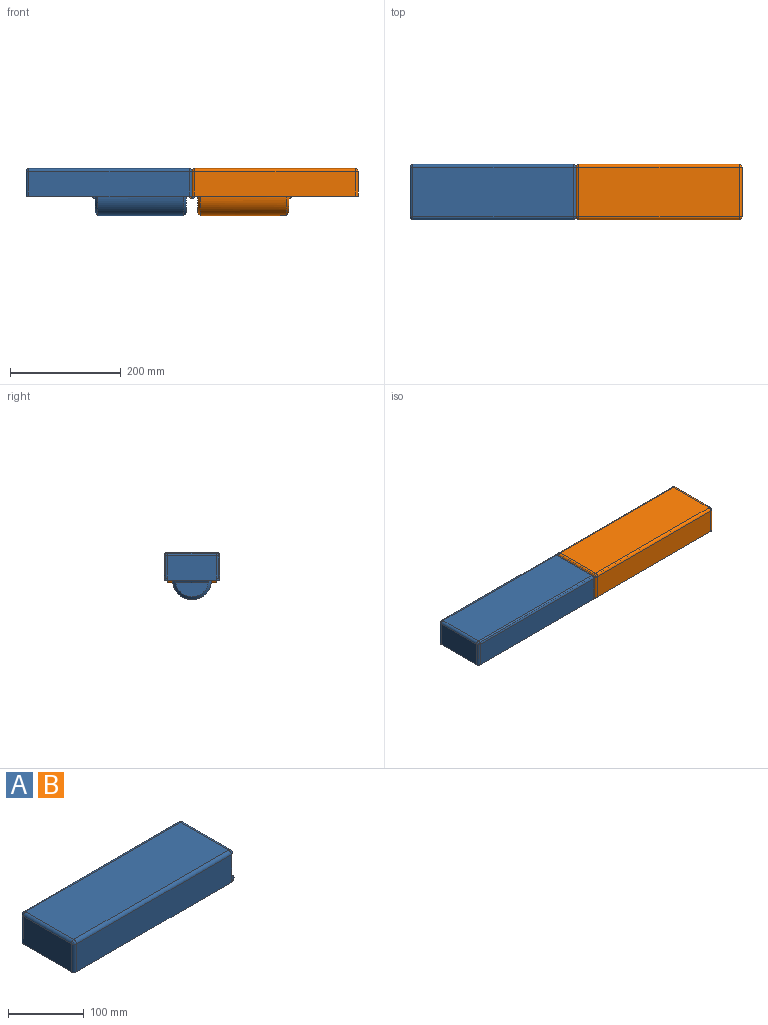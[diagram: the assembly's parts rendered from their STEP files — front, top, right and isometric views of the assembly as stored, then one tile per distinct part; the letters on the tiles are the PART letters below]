
ASSEMBLY  parts=2 mates=1
PART A: 72 faces, bbox 305x100x85 mm
  f0: plane 59.28x25.37mm, normal (-1,0,0), area 1137.1mm2, adj f18,f65
  f1: plane 9.26x0.36mm, normal (-1,0,0), area 2.2mm2, adj f18,f64
  f2: plane 9.26x0.36mm, normal (-1,0,0), area 2.2mm2, adj f18,f63
  f3: plane 45x37.5mm, normal (0,1,0), area 361.4mm2, adj f21,f22,f23,f25,f43,f44,f45,f46
  f4: plane 80x40mm, normal (-1,0,0), area 1275.8mm2, adj f10,f11,f13,f14,f15
  f5: plane 90x40mm, normal (1,0,0), area 3600mm2, adj f53,f59,f62,f70
  f6: plane 290x45mm, normal (0,1,0), area 13050mm2, adj f10,f56,f60,f62
  f7: plane 90x45mm, normal (-1,0,0), area 4050mm2, adj f10,f51,f55,f56
  f8: plane 290x45mm, normal (0,-1,0), area 13050mm2, adj f10,f51,f53,f54
  f9: plane 290x90mm, normal (0,0,1), area 26100mm2, adj f54,f55,f59,f60
  f10: plane 300x100mm, normal (0,0,-1), area 7603.5mm2, adj f4,f6,f7,f8,f11,f12,f13,f15
  f11: plane 280x40mm, normal (0,-1,0), area 11200mm2, adj f4,f10,f12,f14
  f12: plane 80x40mm, normal (1,0,0), area 2493.1mm2, adj f10,f11,f13,f14,f20
  f13: plane 280x40mm, normal (0,1,0), area 11200mm2, adj f4,f10,f12,f14
  f14: plane 280x80mm, normal (0,0,-1), area 22400mm2, adj f4,f11,f12,f13
  f15: cylinder r=35mm len=160mm, axis (1,0,0), area 34636.1mm2, adj f4,f10,f18,f19
  f16: plane 59.28x25.37mm, normal (-1,0,0), area 1137.1mm2, adj f18,f66
  f17: plane 60x30mm, normal (1,0,0), area 1413.7mm2, adj f10,f19
  f18: cone r=30mm half-angle=45deg, axis (1,0,0), area 1443.9mm2, adj f0,f1,f2,f15,f16
  f19: cone r=35mm half-angle=45deg, axis (-1,0,0), area 722mm2, adj f10,f15,f17
  f20: cylinder r=15mm len=30mm, axis (-1,0,0), area 2827.4mm2, adj f12,f21,f22
  f21: plane 30x18.75mm, normal (-1,0,0), area 209.1mm2, adj f3,f20,f23,f24
  f22: plane 30x18.75mm, normal (-1,0,0), area 209.1mm2, adj f3,f20,f24,f25
  f23: plane 60x30mm, normal (0,0,1), area 1703.4mm2, adj f3,f21,f24,f71
  f24: plane 45x37.5mm, normal (0,-1,0), area 361.4mm2, adj f21,f22,f23,f25,f43,f44,f45,f46
  f25: plane 60x30mm, normal (0,0,-1), area 1703.4mm2, adj f3,f22,f24,f50
  f26: plane 85x40mm, normal (1,0,0), area 1903.2mm2, adj f32,f33,f35,f36,f37
  f27: plane 95x45mm, normal (-1,0,0), area 4275mm2, adj f28,f30,f31,f32
  f28: plane 295x45mm, normal (0,-1,0), area 13275mm2, adj f27,f29,f31,f32
  f29: plane 95x45mm, normal (1,0,0), area 4275mm2, adj f28,f30,f31,f32
  f30: plane 295x45mm, normal (0,1,0), area 13275mm2, adj f27,f29,f31,f32
  f31: plane 295x95mm, normal (0,0,-1), area 28025mm2, adj f27,f28,f29,f30
  f32: plane 295.02x95.02mm, normal (0,0,1), area 4136.6mm2, adj f26,f27,f28,f29,f30,f33,f34,f35
  f33: plane 285x40mm, normal (0,1,0), area 11400mm2, adj f26,f32,f34,f36
  f34: plane 85x40mm, normal (-1,0,0), area 2909.1mm2, adj f32,f33,f35,f36,f42
  f35: plane 285x40mm, normal (0,-1,0), area 11400mm2, adj f26,f32,f34,f36
  f36: plane 285x85mm, normal (0,0,1), area 24225mm2, adj f26,f33,f34,f35
  f37: cylinder r=32.5mm len=161.46mm, axis (1,0,0), area 32057.4mm2, adj f26,f32,f40,f41
  f38: plane 57.93x57.93mm, normal (1,0,0), area 2635.6mm2, adj f40
  f39: plane 57.93x31.46mm, normal (-1,0,0), area 1462.4mm2, adj f32,f41
  f40: cone r=28.23mm half-angle=45deg, axis (1,0,0), area 965.5mm2, adj f37,f38
  f41: cone r=33.23mm half-angle=45deg, axis (-1,0,0), area 507.8mm2, adj f32,f37,f39
  f42: cylinder r=12.5mm len=35mm, axis (-1,0,0), area 2748.9mm2, adj f34,f43
  f43: plane 32.5x30mm, normal (1,0,0), area 484.1mm2, adj f3,f24,f42,f44,f45
  f44: plane 30x13.38mm, normal (0,0,-1), area 333.1mm2, adj f3,f24,f43,f46
  f45: plane 57.5x30mm, normal (0,0,1), area 1628.4mm2, adj f3,f24,f43,f50
  f46: cylinder r=35mm len=30mm, axis (0,0,1), area 465.1mm2, adj f3,f24,f44,f49
  f47: plane 40x40mm, normal (0,0,-1), area 1256.6mm2, adj f49
  f48: plane 40x33.23mm, normal (0,0,1), area 440.6mm2, adj f3,f24,f49,f71
  f49: torus R=20mm, axis (0,0,-1), area 8003.1mm2, adj f3,f24,f46,f47,f48
  f50: cylinder r=15mm len=30mm, axis (0,0,-1), area 117.8mm2, adj f3,f24,f25,f45
  f51: cylinder r=5mm len=45mm, axis (0,0,-1), area 353.4mm2, adj f7,f8,f10,f52
  f52: sphere r=5mm, area 39.3mm2, adj f51,f54,f55
  f53: cylinder r=5mm len=45mm, axis (0,0,1), area 353.4mm2, adj f5,f8,f10,f57,f69
  f54: cylinder r=5mm len=290mm, axis (-1,0,0), area 2277.7mm2, adj f8,f9,f52,f57
  f55: cylinder r=5mm len=90mm, axis (0,1,0), area 706.9mm2, adj f7,f9,f52,f58
  f56: cylinder r=5mm len=45mm, axis (0,0,1), area 353.4mm2, adj f6,f7,f10,f58
  f57: sphere r=5mm, area 39.3mm2, adj f53,f54,f59
  f58: sphere r=5mm, area 39.3mm2, adj f55,f56,f60
  f59: cylinder r=5mm len=90mm, axis (0,-1,0), area 706.9mm2, adj f5,f9,f57,f61
  f60: cylinder r=5mm len=290mm, axis (1,0,0), area 2277.7mm2, adj f6,f9,f58,f61
  f61: sphere r=5mm, area 39.3mm2, adj f59,f60,f62
  f62: cylinder r=5mm len=45mm, axis (0,0,-1), area 353.4mm2, adj f5,f6,f10,f61,f68
  f63: plane 9.26x4.99mm, normal (0,1,0), area 35.6mm2, adj f2,f65,f66
  f64: plane 9.26x4.99mm, normal (0,-1,0), area 35.6mm2, adj f1,f65,f66
  f65: cylinder r=5mm len=59.28mm, axis (0,-1,0), area 443.5mm2, adj f0,f63,f64,f66
  f66: cylinder r=5mm len=59.28mm, axis (0,1,0), area 443.5mm2, adj f16,f63,f64,f65
  f67: plane 90x5mm, normal (-1,0,0), area 450mm2, adj f10,f68,f69,f70
  f68: plane 10x5mm, normal (0,1,0), area 39.3mm2, adj f62,f67,f70
  f69: plane 10x5mm, normal (0,-1,0), area 39.3mm2, adj f53,f67,f70
  f70: cylinder r=5mm len=90mm, axis (0,1,0), area 1413.7mm2, adj f5,f67,f68,f69
  f71: cylinder r=15mm len=30mm, axis (0,0,-1), area 117.8mm2, adj f3,f23,f24,f48
PART B: same geometry as A
PLACE A t=(-660.23,-24.83,-30.35)mm
PLACE B rot(axis=(0,0,1),180deg) t=(-360.23,-24.83,-30.35)mm
MATE revolute B.f70 <-> A.f70  axis (0,-1,0) through (-510.23,-24.83,-30.35)mm
